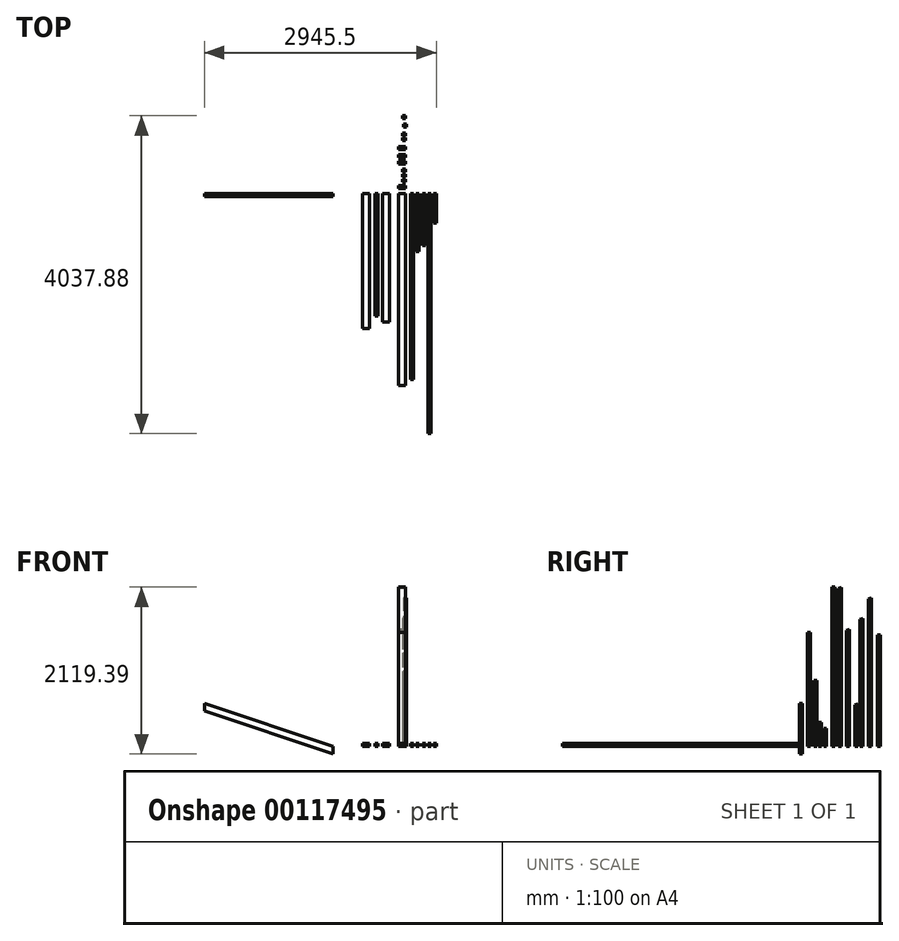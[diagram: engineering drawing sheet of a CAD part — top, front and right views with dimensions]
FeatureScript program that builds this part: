
annotation { "Feature Type Name" : "Feature", "Feature Type Description" : "" }
export const myFeature = defineFeature(function(context is Context, id is Id, definition is map)
    precondition{}
    {
        {
            var Q0;
            Q0=qCreatedBy(makeId("Front.planeOp"),FACE);
            var sketch = newSketch(context, id + "F0", { "sketchPlane" : qUnion([Q0])});
            skLineSegment(sketch, "E0.bottom", {"start": v(0, 0) * mm, "end": v(-88.9, 0) * mm});
            skLineSegment(sketch, "E0.top", {"start": v(0, 38.1) * mm, "end": v(-88.9, 38.1) * mm});
            skLineSegment(sketch, "E0.left", {"start": v(0, 0) * mm, "end": v(0, 38.1) * mm});
            skLineSegment(sketch, "E0.right", {"start": v(-88.9, 0) * mm, "end": v(-88.9, 38.1) * mm});
            skSolve(sketch);
        }
        {
            var Q0;
            Q0=makeQuery(id+"F0.imprint","IMPRINT",FACE,{"disambiguationData":[TD([[makeQuery(id+"F0.imprint","IMPRINT",EDGE,{"derivedFrom":sQuery(id+"F0.wireOp",EDGE,"E0.bottom")}),-1.0]])]});
            extrude(context, id + "F1", {"entities" : qUnion([Q0]), "depth" : 2438.4 * mm});
        }
        {
            var Q0;
            Q0=qCreatedBy(makeId("Top.planeOp"),FACE);
            var sketch = newSketch(context, id + "F2", { "sketchPlane" : qUnion([Q0])});
            skLineSegment(sketch, "E1.bottom", {"start": v(0, 63.95) * mm, "end": v(-88.9, 63.95) * mm});
            skLineSegment(sketch, "E1.top", {"start": v(0, 102.05) * mm, "end": v(-88.9, 102.05) * mm});
            skLineSegment(sketch, "E1.left", {"start": v(0, 63.95) * mm, "end": v(0, 102.05) * mm});
            skLineSegment(sketch, "E1.right", {"start": v(-88.9, 63.95) * mm, "end": v(-88.9, 102.05) * mm});
            skSolve(sketch);
        }
        {
            var Q0;
            Q0=makeQuery(id+"F2.imprint","IMPRINT",FACE,{"disambiguationData":[TD([[makeQuery(id+"F2.imprint","IMPRINT",EDGE,{"derivedFrom":sQuery(id+"F2.wireOp",EDGE,"E1.bottom")}),-1.0]])]});
            extrude(context, id + "F3", {"entities" : qUnion([Q0]), "depth" : 1447.8 * mm});
        }
        {
            var Q0;
            Q0=qCreatedBy(makeId("Front.planeOp"),FACE);
            var sketch = newSketch(context, id + "F4", { "sketchPlane" : qUnion([Q0])});
            skLineSegment(sketch, "E2.bottom", {"start": v(59.34, 0) * mm, "end": v(97.44, 0) * mm});
            skLineSegment(sketch, "E2.top", {"start": v(59.34, 38.1) * mm, "end": v(97.44, 38.1) * mm});
            skLineSegment(sketch, "E2.left", {"start": v(59.34, 0) * mm, "end": v(59.34, 38.1) * mm});
            skLineSegment(sketch, "E2.right", {"start": v(97.44, 0) * mm, "end": v(97.44, 38.1) * mm});
            skSolve(sketch);
        }
        {
            var Q0;
            Q0=makeQuery(id+"F4.imprint","IMPRINT",FACE,{"disambiguationData":[TD([[makeQuery(id+"F4.imprint","IMPRINT",EDGE,{"derivedFrom":sQuery(id+"F4.wireOp",EDGE,"E2.bottom")}),1.0]])]});
            extrude(context, id + "F5", {"entities" : qUnion([Q0]), "depth" : 2362.2 * mm});
        }
        {
            var Q0;
            Q0=qCreatedBy(makeId("Top.planeOp"),FACE);
            var sketch = newSketch(context, id + "F6", { "sketchPlane" : qUnion([Q0])});
            skLineSegment(sketch, "E3.bottom", {"start": v(0, 145.9) * mm, "end": v(-38.1, 145.9) * mm});
            skLineSegment(sketch, "E3.top", {"start": v(0, 184) * mm, "end": v(-38.1, 184) * mm});
            skLineSegment(sketch, "E3.left", {"start": v(0, 145.9) * mm, "end": v(0, 184) * mm});
            skLineSegment(sketch, "E3.right", {"start": v(-38.1, 145.9) * mm, "end": v(-38.1, 184) * mm});
            skSolve(sketch);
        }
        {
            var Q0;
            Q0=makeQuery(id+"F6.imprint","IMPRINT",FACE,{"disambiguationData":[TD([[makeQuery(id+"F6.imprint","IMPRINT",EDGE,{"derivedFrom":sQuery(id+"F6.wireOp",EDGE,"E3.bottom")}),-1.0]])]});
            extrude(context, id + "F7", {"entities" : qUnion([Q0]), "depth" : 838.2 * mm});
        }
        {
            var Q0;
            Q0=qCreatedBy(makeId("Top.planeOp"),FACE);
            var sketch = newSketch(context, id + "F8", { "sketchPlane" : qUnion([Q0])});
            skLineSegment(sketch, "E4.bottom", {"start": v(0, 272.01) * mm, "end": v(-38.1, 272.01) * mm});
            skLineSegment(sketch, "E4.top", {"start": v(0, 310.11) * mm, "end": v(-38.1, 310.11) * mm});
            skLineSegment(sketch, "E4.left", {"start": v(0, 272.01) * mm, "end": v(0, 310.11) * mm});
            skLineSegment(sketch, "E4.right", {"start": v(-38.1, 272.01) * mm, "end": v(-38.1, 310.11) * mm});
            skSolve(sketch);
        }
        {
            var Q0;
            Q0=makeQuery(id+"F8.imprint","IMPRINT",FACE,{"disambiguationData":[TD([[makeQuery(id+"F8.imprint","IMPRINT",EDGE,{"derivedFrom":sQuery(id+"F8.wireOp",EDGE,"E4.bottom")}),-1.0]])]});
            extrude(context, id + "F9", {"entities" : qUnion([Q0]), "depth" : 228.6 * mm});
        }
        {
            var Q0;
            Q0=qCreatedBy(makeId("Top.planeOp"),FACE);
            var sketch = newSketch(context, id + "F10", { "sketchPlane" : qUnion([Q0])});
            skLineSegment(sketch, "E5.bottom", {"start": v(0, 206.85) * mm, "end": v(-38.1, 206.85) * mm});
            skLineSegment(sketch, "E5.top", {"start": v(0, 244.95) * mm, "end": v(-38.1, 244.95) * mm});
            skLineSegment(sketch, "E5.left", {"start": v(0, 206.85) * mm, "end": v(0, 244.95) * mm});
            skLineSegment(sketch, "E5.right", {"start": v(-38.1, 206.85) * mm, "end": v(-38.1, 244.95) * mm});
            skSolve(sketch);
        }
        {
            var Q0;
            Q0=makeQuery(id+"F10.imprint","IMPRINT",FACE,{"disambiguationData":[TD([[makeQuery(id+"F10.imprint","IMPRINT",EDGE,{"derivedFrom":sQuery(id+"F10.wireOp",EDGE,"E5.bottom")}),-1.0]])]});
            extrude(context, id + "F11", {"entities" : qUnion([Q0]), "depth" : 304.8 * mm});
        }
        {
            var Q0;
            Q0=qCreatedBy(makeId("Top.planeOp"),FACE);
            var sketch = newSketch(context, id + "F12", { "sketchPlane" : qUnion([Q0])});
            skLineSegment(sketch, "E6.bottom", {"start": v(0, 376.3) * mm, "end": v(-88.9, 376.3) * mm});
            skLineSegment(sketch, "E6.top", {"start": v(0, 414.4) * mm, "end": v(-88.9, 414.4) * mm});
            skLineSegment(sketch, "E6.left", {"start": v(0, 376.3) * mm, "end": v(0, 414.4) * mm});
            skLineSegment(sketch, "E6.right", {"start": v(-88.9, 376.3) * mm, "end": v(-88.9, 414.4) * mm});
            skSolve(sketch);
        }
        {
            var Q0;
            Q0=makeQuery(id+"F12.imprint","IMPRINT",FACE,{"disambiguationData":[TD([[makeQuery(id+"F12.imprint","IMPRINT",EDGE,{"derivedFrom":sQuery(id+"F12.wireOp",EDGE,"E6.bottom")}),-1.0]])]});
            extrude(context, id + "F13", {"entities" : qUnion([Q0]), "depth" : 2025.65 * mm});
        }
        {
            var Q0;
            Q0=qCreatedBy(makeId("Front.planeOp"),FACE);
            var sketch = newSketch(context, id + "F14", { "sketchPlane" : qUnion([Q0])});
            skLineSegment(sketch, "E7.bottom", {"start": v(-204.26, 0) * mm, "end": v(-293.16, 0) * mm});
            skLineSegment(sketch, "E7.top", {"start": v(-204.26, 38.1) * mm, "end": v(-293.16, 38.1) * mm});
            skLineSegment(sketch, "E7.left", {"start": v(-204.26, 0) * mm, "end": v(-204.26, 38.1) * mm});
            skLineSegment(sketch, "E7.right", {"start": v(-293.16, 0) * mm, "end": v(-293.16, 38.1) * mm});
            skSolve(sketch);
        }
        {
            var Q0;
            Q0=makeQuery(id+"F14.imprint","IMPRINT",FACE,{"disambiguationData":[TD([[makeQuery(id+"F14.imprint","IMPRINT",EDGE,{"derivedFrom":sQuery(id+"F14.wireOp",EDGE,"E7.bottom")}),-1.0]])]});
            extrude(context, id + "F15", {"entities" : qUnion([Q0]), "depth" : 1631.95 * mm});
        }
        {
            var Q0;
            Q0=qCreatedBy(makeId("Front.planeOp"),FACE);
            var sketch = newSketch(context, id + "F16", { "sketchPlane" : qUnion([Q0])});
            skLineSegment(sketch, "E8.bottom", {"start": v(-350.36, 0) * mm, "end": v(-388.46, 0) * mm});
            skLineSegment(sketch, "E8.top", {"start": v(-350.36, 38.1) * mm, "end": v(-388.46, 38.1) * mm});
            skLineSegment(sketch, "E8.left", {"start": v(-350.36, 0) * mm, "end": v(-350.36, 38.1) * mm});
            skLineSegment(sketch, "E8.right", {"start": v(-388.46, 0) * mm, "end": v(-388.46, 38.1) * mm});
            skSolve(sketch);
        }
        {
            var Q0;
            Q0=makeQuery(id+"F16.imprint","IMPRINT",FACE,{"disambiguationData":[TD([[makeQuery(id+"F16.imprint","IMPRINT",EDGE,{"derivedFrom":sQuery(id+"F16.wireOp",EDGE,"E8.bottom")}),-1.0]])]});
            extrude(context, id + "F17", {"entities" : qUnion([Q0]), "depth" : 1555.75 * mm});
        }
        {
            var Q0;
            Q0=qCreatedBy(makeId("Top.planeOp"),FACE);
            var sketch = newSketch(context, id + "F18", { "sketchPlane" : qUnion([Q0])});
            skLineSegment(sketch, "E9.bottom", {"start": v(0, 459.55) * mm, "end": v(-88.9, 459.55) * mm});
            skLineSegment(sketch, "E9.top", {"start": v(0, 497.65) * mm, "end": v(-88.9, 497.65) * mm});
            skLineSegment(sketch, "E9.left", {"start": v(0, 459.55) * mm, "end": v(0, 497.65) * mm});
            skLineSegment(sketch, "E9.right", {"start": v(-88.9, 459.55) * mm, "end": v(-88.9, 497.65) * mm});
            skSolve(sketch);
        }
        {
            var Q0;
            Q0=makeQuery(id+"F18.imprint","IMPRINT",FACE,{"disambiguationData":[TD([[makeQuery(id+"F18.imprint","IMPRINT",EDGE,{"derivedFrom":sQuery(id+"F18.wireOp",EDGE,"E9.bottom")}),-1.0]])]});
            extrude(context, id + "F19", {"entities" : qUnion([Q0]), "depth" : 2022.47 * mm});
        }
        {
            var Q0;
            Q0=makeQuery(id+"F19.opExtrude","SWEPT_FACE",FACE,{"disambiguationData":[OSD([sQuery(id+"F18.wireOp",EDGE,"E9.right")])]});
            var sketch = newSketch(context, id + "F20", { "sketchPlane" : qUnion([Q0])});
            skLineSegment(sketch, "E10", {"start": v(-497.65, 2022.47) * mm, "end": v(-459.55, 2009.77) * mm});
            skLineSegment(sketch, "E11", {"start": v(-459.55, 2009.77) * mm, "end": v(-459.55, 2022.47) * mm});
            skLineSegment(sketch, "E12", {"start": v(-459.55, 2022.47) * mm, "end": v(-497.65, 2022.47) * mm});
            skSolve(sketch);
        }
        {
            var Q0;
            Q0=makeQuery(id+"F20.imprint","IMPRINT",FACE,{"disambiguationData":[TD([[makeQuery(id+"F20.imprint","IMPRINT",EDGE,{"derivedFrom":sQuery(id+"F20.wireOp",EDGE,"E10")}),1.0]])]});
            extrude(context, id + "F21", {"entities" : qUnion([Q0]), "operationType" : NewBodyOperationType.REMOVE, "oppositeDirection" : true, "depth" : 88.9 * mm});
        }
        {
            var Q0;
            Q0=qCreatedBy(makeId("Top.planeOp"),FACE);
            var sketch = newSketch(context, id + "F22", { "sketchPlane" : qUnion([Q0])});
            skLineSegment(sketch, "E13.bottom", {"start": v(0, 558.67) * mm, "end": v(-88.9, 558.67) * mm});
            skLineSegment(sketch, "E13.top", {"start": v(0, 596.77) * mm, "end": v(-88.9, 596.77) * mm});
            skLineSegment(sketch, "E13.left", {"start": v(0, 558.67) * mm, "end": v(0, 596.77) * mm});
            skLineSegment(sketch, "E13.right", {"start": v(-88.9, 558.67) * mm, "end": v(-88.9, 596.77) * mm});
            skSolve(sketch);
        }
        {
            var Q0;
            Q0=makeQuery(id+"F22.imprint","IMPRINT",FACE,{"disambiguationData":[TD([[makeQuery(id+"F22.imprint","IMPRINT",EDGE,{"derivedFrom":sQuery(id+"F22.wireOp",EDGE,"E13.bottom")}),-1.0]])]});
            extrude(context, id + "F23", {"entities" : qUnion([Q0]), "depth" : 1489.07 * mm});
        }
        {
            var Q0;
            Q0=makeQuery(id+"F23.opExtrude","SWEPT_FACE",FACE,{"disambiguationData":[OSD([sQuery(id+"F22.wireOp",EDGE,"E13.right")])]});
            var sketch = newSketch(context, id + "F24", { "sketchPlane" : qUnion([Q0])});
            skLineSegment(sketch, "E14", {"start": v(-596.77, 1489.08) * mm, "end": v(-558.67, 1476.38) * mm});
            skLineSegment(sketch, "E15", {"start": v(-558.67, 1476.38) * mm, "end": v(-558.67, 1489.08) * mm});
            skLineSegment(sketch, "E16", {"start": v(-558.67, 1489.08) * mm, "end": v(-596.77, 1489.08) * mm});
            skSolve(sketch);
        }
        {
            var Q0;
            Q0=makeQuery(id+"F24.imprint","IMPRINT",FACE,{"disambiguationData":[TD([[makeQuery(id+"F24.imprint","IMPRINT",EDGE,{"derivedFrom":sQuery(id+"F24.wireOp",EDGE,"E14")}),1.0]])]});
            extrude(context, id + "F25", {"entities" : qUnion([Q0]), "operationType" : NewBodyOperationType.REMOVE, "oppositeDirection" : true, "depth" : 88.9 * mm});
        }
        {
            var Q0;
            Q0=qCreatedBy(makeId("Front.planeOp"),FACE);
            var sketch = newSketch(context, id + "F26", { "sketchPlane" : qUnion([Q0])});
            skLineSegment(sketch, "E17.bottom", {"start": v(-457.71, 0) * mm, "end": v(-546.61, 0) * mm});
            skLineSegment(sketch, "E17.top", {"start": v(-457.71, 38.1) * mm, "end": v(-546.61, 38.1) * mm});
            skLineSegment(sketch, "E17.left", {"start": v(-457.71, 0) * mm, "end": v(-457.71, 38.1) * mm});
            skLineSegment(sketch, "E17.right", {"start": v(-546.61, 0) * mm, "end": v(-546.61, 38.1) * mm});
            skSolve(sketch);
        }
        {
            var Q0;
            Q0=makeQuery(id+"F26.imprint","IMPRINT",FACE,{"disambiguationData":[TD([[makeQuery(id+"F26.imprint","IMPRINT",EDGE,{"derivedFrom":sQuery(id+"F26.wireOp",EDGE,"E17.bottom")}),-1.0]])]});
            extrude(context, id + "F27", {"entities" : qUnion([Q0]), "depth" : 1714.5 * mm});
        }
        {
            var Q0;
            Q0=qCreatedBy(makeId("Top.planeOp"),FACE);
            var sketch = newSketch(context, id + "F28", { "sketchPlane" : qUnion([Q0])});
            skLineSegment(sketch, "E18.bottom", {"start": v(0, 671.46) * mm, "end": v(-38.1, 671.46) * mm});
            skLineSegment(sketch, "E18.top", {"start": v(0, 709.56) * mm, "end": v(-38.1, 709.56) * mm});
            skLineSegment(sketch, "E18.left", {"start": v(0, 671.46) * mm, "end": v(0, 709.56) * mm});
            skLineSegment(sketch, "E18.right", {"start": v(-38.1, 671.46) * mm, "end": v(-38.1, 709.56) * mm});
            skSolve(sketch);
        }
        {
            var Q0;
            Q0=makeQuery(id+"F28.imprint","IMPRINT",FACE,{"disambiguationData":[TD([[makeQuery(id+"F28.imprint","IMPRINT",EDGE,{"derivedFrom":sQuery(id+"F28.wireOp",EDGE,"E18.bottom")}),-1.0]])]});
            extrude(context, id + "F29", {"entities" : qUnion([Q0]), "depth" : 539.75 * mm});
        }
        {
            var Q0;
            Q0=makeQuery(id+"F29.opExtrude","SWEPT_FACE",FACE,{"disambiguationData":[OSD([sQuery(id+"F28.wireOp",EDGE,"E18.right")])]});
            var sketch = newSketch(context, id + "F30", { "sketchPlane" : qUnion([Q0])});
            skLineSegment(sketch, "E19", {"start": v(-709.56, 539.75) * mm, "end": v(-671.46, 527.05) * mm});
            skLineSegment(sketch, "E20", {"start": v(-671.46, 527.05) * mm, "end": v(-671.46, 539.75) * mm});
            skLineSegment(sketch, "E21", {"start": v(-671.46, 539.75) * mm, "end": v(-709.56, 539.75) * mm});
            skSolve(sketch);
        }
        {
            var Q0;
            Q0=makeQuery(id+"F30.imprint","IMPRINT",FACE,{"disambiguationData":[TD([[makeQuery(id+"F30.imprint","IMPRINT",EDGE,{"derivedFrom":sQuery(id+"F30.wireOp",EDGE,"E19")}),1.0]])]});
            extrude(context, id + "F31", {"entities" : qUnion([Q0]), "operationType" : NewBodyOperationType.REMOVE, "oppositeDirection" : true, "depth" : 38.1 * mm});
        }
        {
            var Q0;
            Q0=qCreatedBy(makeId("Front.planeOp"),FACE);
            var sketch = newSketch(context, id + "F32", { "sketchPlane" : qUnion([Q0])});
            skLineSegment(sketch, "E22", {"start": v(-922.97, 0) * mm, "end": v(-2554.9, 546.03) * mm});
            skLineSegment(sketch, "E23", {"start": v(-2554.9, 546.03) * mm, "end": v(-2554.9, 452.29) * mm});
            skLineSegment(sketch, "E24", {"start": v(-2554.9, 452.29) * mm, "end": v(-922.97, -93.74) * mm});
            skLineSegment(sketch, "E25", {"start": v(-922.97, -93.74) * mm, "end": v(-922.97, 0) * mm});
            skSolve(sketch);
        }
        {
            var Q0;
            Q0=makeQuery(id+"F32.imprint","IMPRINT",FACE,{"disambiguationData":[TD([[makeQuery(id+"F32.imprint","IMPRINT",EDGE,{"derivedFrom":sQuery(id+"F32.wireOp",EDGE,"E22")}),1.0]])]});
            extrude(context, id + "F33", {"entities" : qUnion([Q0]), "depth" : 38.1 * mm});
        }
        {
            var Q0;
            Q0=qCreatedBy(makeId("Top.planeOp"),FACE);
            var sketch = newSketch(context, id + "F34", { "sketchPlane" : qUnion([Q0])});
            skLineSegment(sketch, "E26.bottom", {"start": v(0, 730.92) * mm, "end": v(-38.1, 730.92) * mm});
            skLineSegment(sketch, "E26.top", {"start": v(0, 769.02) * mm, "end": v(-38.1, 769.02) * mm});
            skLineSegment(sketch, "E26.left", {"start": v(0, 730.92) * mm, "end": v(0, 769.02) * mm});
            skLineSegment(sketch, "E26.right", {"start": v(-38.1, 730.92) * mm, "end": v(-38.1, 769.02) * mm});
            skSolve(sketch);
        }
        {
            var Q0;
            Q0=makeQuery(id+"F34.imprint","IMPRINT",FACE,{"disambiguationData":[TD([[makeQuery(id+"F34.imprint","IMPRINT",EDGE,{"derivedFrom":sQuery(id+"F34.wireOp",EDGE,"E26.bottom")}),-1.0]])]});
            extrude(context, id + "F35", {"entities" : qUnion([Q0]), "depth" : 1625.6 * mm});
        }
        {
            var Q0;
            Q0=qCreatedBy(makeId("Top.planeOp"),FACE);
            var sketch = newSketch(context, id + "F36", { "sketchPlane" : qUnion([Q0])});
            skLineSegment(sketch, "E27.bottom", {"start": v(9.97, 842.7) * mm, "end": v(-28.13, 842.7) * mm});
            skLineSegment(sketch, "E27.top", {"start": v(9.97, 880.8) * mm, "end": v(-28.13, 880.8) * mm});
            skLineSegment(sketch, "E27.left", {"start": v(9.97, 842.7) * mm, "end": v(9.97, 880.8) * mm});
            skLineSegment(sketch, "E27.right", {"start": v(-28.13, 842.7) * mm, "end": v(-28.13, 880.8) * mm});
            skSolve(sketch);
        }
        {
            var Q0;
            Q0 = qSketchRegion(id + "F36", true);
            extrude(context, id + "F37", {"entities" : qUnion([Q0]), "depth" : 1885.95 * mm});
        }
        {
            var Q0;
            Q0=makeQuery(id+"F37.opExtrude","SWEPT_FACE",FACE,{"disambiguationData":[OSD([sQuery(id+"F36.wireOp",EDGE,"E27.right")])]});
            var sketch = newSketch(context, id + "F38", { "sketchPlane" : qUnion([Q0])});
            skLineSegment(sketch, "E28", {"start": v(-880.8, 1885.95) * mm, "end": v(-842.7, 1873.25) * mm});
            skLineSegment(sketch, "E29", {"start": v(-842.7, 1873.25) * mm, "end": v(-842.7, 1885.95) * mm});
            skLineSegment(sketch, "E30", {"start": v(-842.7, 1885.95) * mm, "end": v(-880.8, 1885.95) * mm});
            skSolve(sketch);
        }
        {
            var Q0;
            Q0=makeQuery(id+"F38.imprint","IMPRINT",FACE,{"disambiguationData":[TD([[makeQuery(id+"F38.imprint","IMPRINT",EDGE,{"derivedFrom":sQuery(id+"F38.wireOp",EDGE,"E28")}),1.0]])]});
            extrude(context, id + "F39", {"entities" : qUnion([Q0]), "operationType" : NewBodyOperationType.REMOVE, "oppositeDirection" : true, "depth" : 38.1 * mm});
        }
        {
            var Q0;
            Q0=makeQuery(id+"F35.opExtrude","SWEPT_FACE",FACE,{"disambiguationData":[OSD([sQuery(id+"F34.wireOp",EDGE,"E26.right")])]});
            var sketch = newSketch(context, id + "F40", { "sketchPlane" : qUnion([Q0])});
            skLineSegment(sketch, "E31", {"start": v(-769.02, 1625.6) * mm, "end": v(-730.92, 1612.9) * mm});
            skLineSegment(sketch, "E32", {"start": v(-730.92, 1612.9) * mm, "end": v(-730.92, 1625.6) * mm});
            skLineSegment(sketch, "E33", {"start": v(-730.92, 1625.6) * mm, "end": v(-769.02, 1625.6) * mm});
            skSolve(sketch);
        }
        {
            var Q0;
            Q0=makeQuery(id+"F40.imprint","IMPRINT",FACE,{"disambiguationData":[TD([[makeQuery(id+"F40.imprint","IMPRINT",EDGE,{"derivedFrom":sQuery(id+"F40.wireOp",EDGE,"E31")}),1.0]])]});
            extrude(context, id + "F41", {"entities" : qUnion([Q0]), "operationType" : NewBodyOperationType.REMOVE, "oppositeDirection" : true, "depth" : 38.1 * mm});
        }
        {
            var Q0;
            Q0=qCreatedBy(makeId("Front.planeOp"),FACE);
            var sketch = newSketch(context, id + "F42", { "sketchPlane" : qUnion([Q0])});
            skLineSegment(sketch, "E34.bottom", {"start": v(130.45, 0) * mm, "end": v(168.55, 0) * mm});
            skLineSegment(sketch, "E34.top", {"start": v(130.45, 38.1) * mm, "end": v(168.55, 38.1) * mm});
            skLineSegment(sketch, "E34.left", {"start": v(130.45, 0) * mm, "end": v(130.45, 38.1) * mm});
            skLineSegment(sketch, "E34.right", {"start": v(168.55, 0) * mm, "end": v(168.55, 38.1) * mm});
            skSolve(sketch);
        }
        {
            var Q0;
            Q0=makeQuery(id+"F42.imprint","IMPRINT",FACE,{"disambiguationData":[TD([[makeQuery(id+"F42.imprint","IMPRINT",EDGE,{"derivedFrom":sQuery(id+"F42.wireOp",EDGE,"E34.bottom")}),1.0]])]});
            extrude(context, id + "F43", {"entities" : qUnion([Q0]), "depth" : 736.6 * mm});
        }
        {
            var Q0;
            Q0=qCreatedBy(makeId("Front.planeOp"),FACE);
            var sketch = newSketch(context, id + "F44", { "sketchPlane" : qUnion([Q0])});
            skLineSegment(sketch, "E35.bottom", {"start": v(250.95, 1.56) * mm, "end": v(212.85, 1.56) * mm});
            skLineSegment(sketch, "E35.top", {"start": v(250.95, 39.66) * mm, "end": v(212.85, 39.66) * mm});
            skLineSegment(sketch, "E35.left", {"start": v(250.95, 1.56) * mm, "end": v(250.95, 39.66) * mm});
            skLineSegment(sketch, "E35.right", {"start": v(212.85, 1.56) * mm, "end": v(212.85, 39.66) * mm});
            skSolve(sketch);
        }
        {
            var Q0;
            Q0=makeQuery(id+"F44.imprint","IMPRINT",FACE,{"disambiguationData":[TD([[makeQuery(id+"F44.imprint","IMPRINT",EDGE,{"derivedFrom":sQuery(id+"F44.wireOp",EDGE,"E35.bottom")}),-1.0]])]});
            extrude(context, id + "F45", {"entities" : qUnion([Q0]), "depth" : 660.4 * mm});
        }
        {
            var Q0;
            Q0=qCreatedBy(makeId("Top.planeOp"),FACE);
            var sketch = newSketch(context, id + "F46", { "sketchPlane" : qUnion([Q0])});
            skLineSegment(sketch, "E36.bottom", {"start": v(-1.84, 951.78) * mm, "end": v(-39.94, 951.78) * mm});
            skLineSegment(sketch, "E36.top", {"start": v(-1.84, 989.88) * mm, "end": v(-39.94, 989.88) * mm});
            skLineSegment(sketch, "E36.left", {"start": v(-1.84, 951.78) * mm, "end": v(-1.84, 989.88) * mm});
            skLineSegment(sketch, "E36.right", {"start": v(-39.94, 951.78) * mm, "end": v(-39.94, 989.88) * mm});
            skSolve(sketch);
        }
        {
            var Q0;
            Q0=makeQuery(id+"F46.imprint","IMPRINT",FACE,{"disambiguationData":[TD([[makeQuery(id+"F46.imprint","IMPRINT",EDGE,{"derivedFrom":sQuery(id+"F46.wireOp",EDGE,"E36.bottom")}),-1.0]])]});
            extrude(context, id + "F47", {"entities" : qUnion([Q0]), "depth" : 1416.05 * mm});
        }
        {
            var Q0;
            Q0=qCreatedBy(makeId("Front.planeOp"),FACE);
            var sketch = newSketch(context, id + "F48", { "sketchPlane" : qUnion([Q0])});
            skLineSegment(sketch, "E37.bottom", {"start": v(287.56, 0) * mm, "end": v(325.66, 0) * mm});
            skLineSegment(sketch, "E37.top", {"start": v(287.56, 38.1) * mm, "end": v(325.66, 38.1) * mm});
            skLineSegment(sketch, "E37.left", {"start": v(287.56, 0) * mm, "end": v(287.56, 38.1) * mm});
            skLineSegment(sketch, "E37.right", {"start": v(325.66, 0) * mm, "end": v(325.66, 38.1) * mm});
            skSolve(sketch);
        }
        {
            var Q0;
            Q0=makeQuery(id+"F48.imprint","IMPRINT",FACE,{"disambiguationData":[TD([[makeQuery(id+"F48.imprint","IMPRINT",EDGE,{"derivedFrom":sQuery(id+"F48.wireOp",EDGE,"E37.bottom")}),1.0]])]});
            extrude(context, id + "F49", {"entities" : qUnion([Q0]), "depth" : 3048 * mm});
        }
        {
            var Q0;
            Q0=qCreatedBy(makeId("Front.planeOp"),FACE);
            var sketch = newSketch(context, id + "F50", { "sketchPlane" : qUnion([Q0])});
            skLineSegment(sketch, "E38.bottom", {"start": v(352.51, 0) * mm, "end": v(390.61, 0) * mm});
            skLineSegment(sketch, "E38.top", {"start": v(352.51, 38.1) * mm, "end": v(390.61, 38.1) * mm});
            skLineSegment(sketch, "E38.left", {"start": v(352.51, 0) * mm, "end": v(352.51, 38.1) * mm});
            skLineSegment(sketch, "E38.right", {"start": v(390.61, 0) * mm, "end": v(390.61, 38.1) * mm});
            skSolve(sketch);
        }
        {
            var Q0;
            Q0=makeQuery(id+"F50.imprint","IMPRINT",FACE,{"disambiguationData":[TD([[makeQuery(id+"F50.imprint","IMPRINT",EDGE,{"derivedFrom":sQuery(id+"F50.wireOp",EDGE,"E38.bottom")}),1.0]])]});
            extrude(context, id + "F51", {"entities" : qUnion([Q0]), "depth" : 371.47 * mm});
        }
    });
